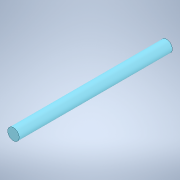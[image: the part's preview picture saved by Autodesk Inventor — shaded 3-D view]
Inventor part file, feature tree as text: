
AUTODESK INVENTOR PART (.ipt)
format: ipt  version: 2022 (Build 260153000, 153)  size: 101,376 bytes
history: native  units: in
note: dims shown in document units (in); Inventor stores cm internally (conversion verified against a paired STEP export)
features: extrude x1, sketch x1
ambient origin geometry x8: Origin, YZ Plane, XZ Plane, XY Plane, X Axis, Y Axis, Z Axis, Center Point
bodies: Solid1 (feature_tree)
feature tree (2):
  extrude  "Extrusion1"  Depth=3.937in
  sketch  "Sketch2"  dims[d0=3.937in d1=0.0in d2=0.2953in]
